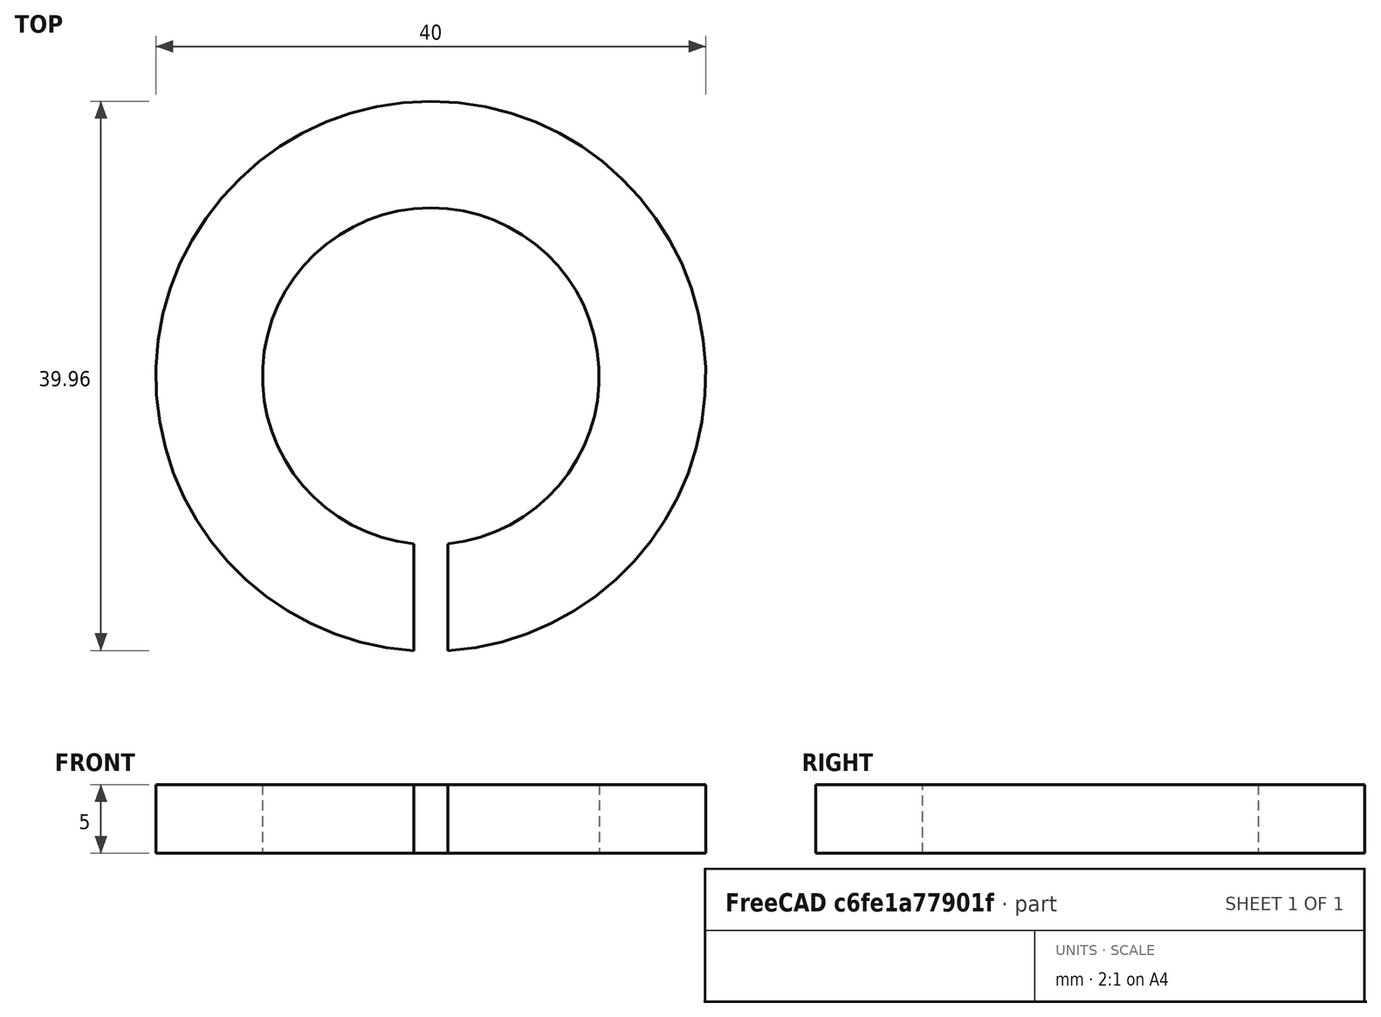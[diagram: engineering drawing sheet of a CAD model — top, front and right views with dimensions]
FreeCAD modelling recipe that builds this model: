
FCSTD DOCUMENT  (FreeCAD 0.15R4651 (Git))
Label: Federring_DIN127-A24
License: All rights reserved
LicenseURL: http://de.wikipedia.org/wiki/Alle_Rechte_vorbehalten
objects: Sketcher::SketchObject×1, PartDesign::Pad×1
note: 3 computed .brp shape members not serialized (recipe doc carries the construction recipe); baked Part::Feature solids carry a one-line shape summary decoded from their .brp

FEATURE [Sketcher::SketchObject] Sketch
  sketch-geometry (4):
    g0: ArcOfCircle CenterX=0 CenterY=0 CenterZ=0 NormalX=0 NormalY=0 NormalZ=1 Radius=12.25 StartAngle=4.81461 EndAngle=10.8934
    g1: ArcOfCircle CenterX=0 CenterY=0 CenterZ=0 NormalX=0 NormalY=0 NormalZ=1 Radius=20 StartAngle=4.77493 EndAngle=10.933
    g2: LineSegment StartX=1.25 StartY=-12.1861 StartZ=0 EndX=1.25 EndY=-19.9609 EndZ=0
    g3: LineSegment StartX=-1.25 StartY=-19.9609 StartZ=0 EndX=-1.25 EndY=-12.1861 EndZ=0
  constraints (12):
    c: Coincident(g0,g-1)
    c: Coincident(g1,g-1)
    c: Vertical(g2)
    c: Vertical(g3)
    c: Coincident(g0,g2)
    c: Coincident(g0,g3)
    c: Coincident(g1,g2)
    c: Coincident(g1,g3)
    c: Symmetric(g1,g1,g-2)
    c: Radius(g0) = 12.25
    c: Radius(g1) = 20
    c: DistanceX(g1,g1) = -2.5
FEATURE [PartDesign::Pad] Pad  label="Federring DIN 127-A 24 #"
  Length = 5
  Length2 = 100
  Midplane = true
  Sketch = -> Sketch
  Type = 0
